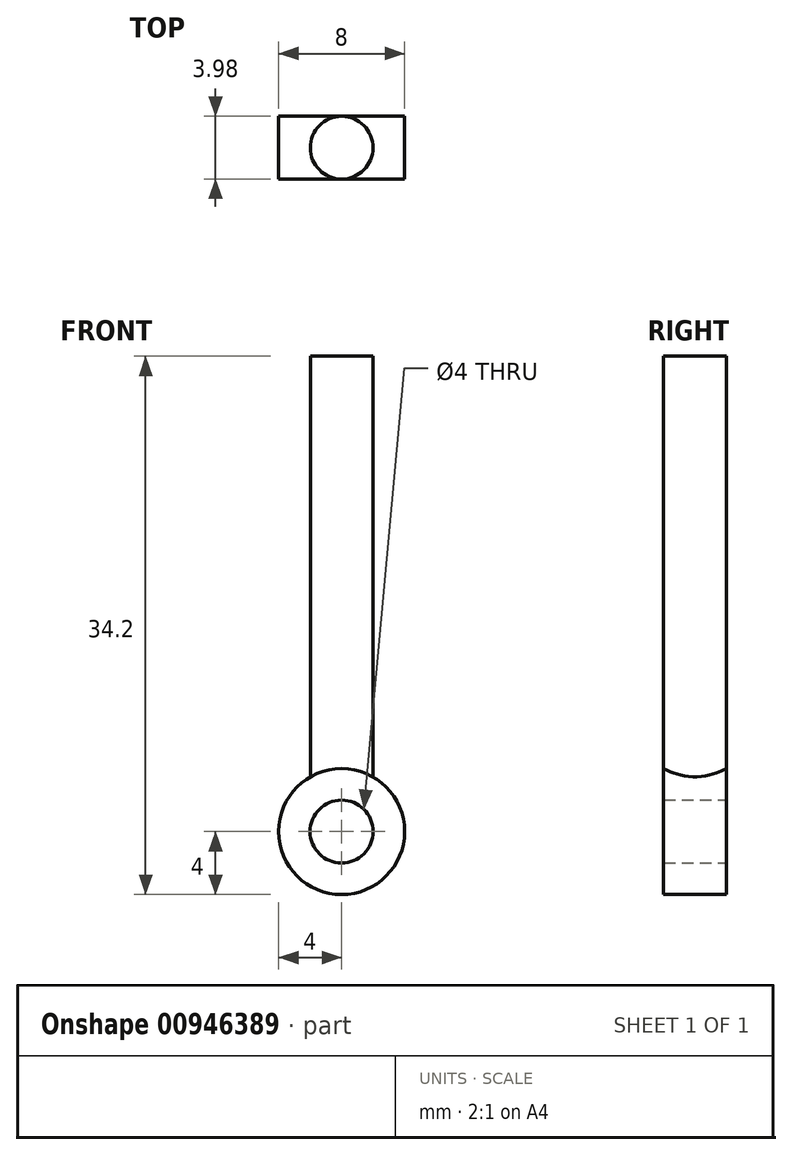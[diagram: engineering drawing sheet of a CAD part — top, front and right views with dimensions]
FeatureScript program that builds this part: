
annotation { "Feature Type Name" : "Feature", "Feature Type Description" : "" }
export const myFeature = defineFeature(function(context is Context, id is Id, definition is map)
    precondition{}
    {
        {
            var Q0;
            Q0=qCreatedBy(makeId("Front.planeOp"),FACE);
            var sketch = newSketch(context, id + "F0", { "sketchPlane" : qUnion([Q0])});
            skCircle(sketch, "E0", {"center": v(0, 0) * mm, "radius": 2 * mm});
            skCircle(sketch, "E1", {"center": v(0, 0) * mm, "radius": 4 * mm});
            skLineSegment(sketch, "E2.top", {"start": v(-2.58, 82.67) * mm, "end": v(2.75, 82.67) * mm});
            skSolve(sketch);
        }
        {
            var Q0;
            Q0=qSketchRegion(id+"F0",true);
            extrude(context, id + "F1", {"entities" : qUnion([Q0]), "endBound" : BoundingType.SYMMETRIC, "depth" : 3.8 * mm, "offsetDistance" : 25 * mm});
        }
        {
            var Q0;
            Q0=qSketchRegion(id+"F0",true);
            extrude(context, id + "F2", {"entities" : qUnion([Q0]), "operationType" : NewBodyOperationType.ADD, "endBound" : BoundingType.SYMMETRIC, "depth" : 3.98 * mm, "offsetDistance" : 25 * mm});
        }
        {
            var Q0;
            Q0=qCreatedBy(makeId("Top.planeOp"),FACE);
            cPlane(context, id + "F3", {"entities" : qUnion([Q0]), "cplaneType" : CPlaneType.OFFSET, "offset" : 2.2 * mm, "width" : 150 * mm, "height" : 150 * mm});
        }
        {
            var Q0;
            Q0=qCreatedBy(id+"F3.planeOp",FACE);
            var sketch = newSketch(context, id + "F4", { "sketchPlane" : qUnion([Q0])});
            skCircle(sketch, "E3", {"center": v(0, 0) * mm, "radius": 1.99 * mm});
            skSolve(sketch);
        }
        {
            var Q0;
            Q0=qSketchRegion(id+"F4",true);
            extrude(context, id + "F5", {"entities" : qUnion([Q0]), "operationType" : NewBodyOperationType.ADD, "depth" : 28 * mm, "offsetDistance" : 25 * mm});
        }
    });
